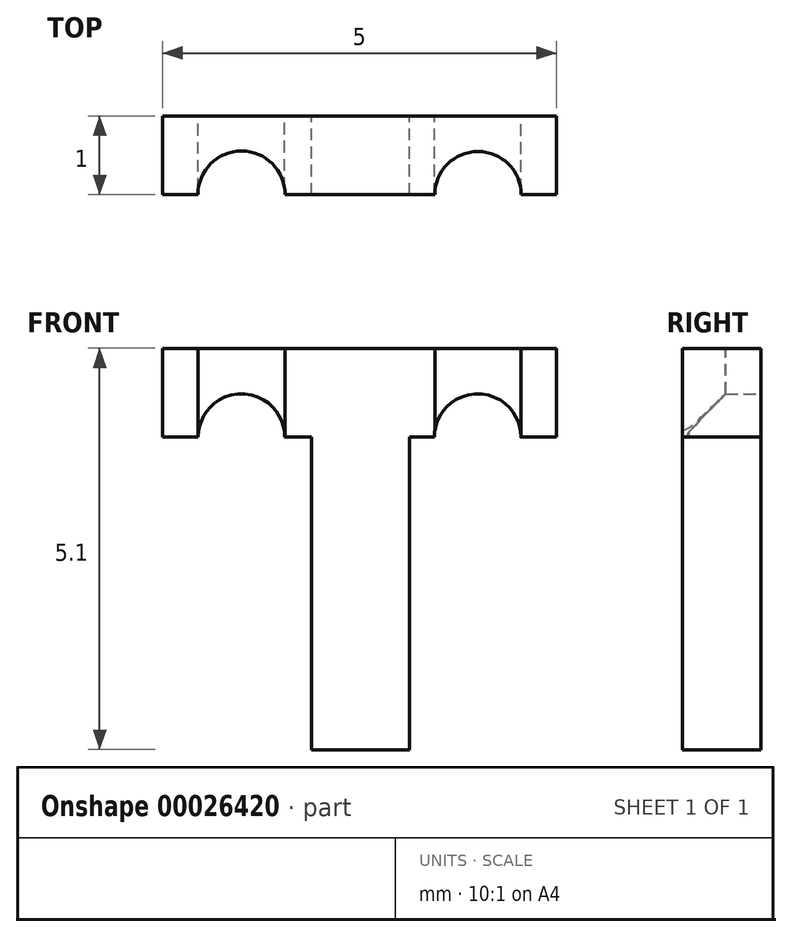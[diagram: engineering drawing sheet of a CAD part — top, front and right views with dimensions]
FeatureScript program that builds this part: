
annotation { "Feature Type Name" : "Feature", "Feature Type Description" : "" }
export const myFeature = defineFeature(function(context is Context, id is Id, definition is map)
    precondition{}
    {
        {
            var Q0;
            Q0=qCreatedBy(makeId("Front.planeOp"),FACE);
            var sketch = newSketch(context, id + "F0", { "sketchPlane" : qUnion([Q0])});
            skArc(sketch, "E0", {"start": v(-0.95, 0) * mm, "mid": v(-1.5, 0.55) * mm, "end": v(-2.05, 0) * mm});
            skArc(sketch, "E1", {"start": v(2.05, 0) * mm, "mid": v(1.5, 0.55) * mm, "end": v(0.95, 0) * mm});
            skLineSegment(sketch, "E2.bottom", {"start": v(-2.5, 0) * mm, "end": v(-2.05, 0) * mm});
            skLineSegment(sketch, "E2.top", {"start": v(-2.5, 1.13) * mm, "end": v(2.5, 1.13) * mm});
            skLineSegment(sketch, "E2.left", {"start": v(-2.5, 0) * mm, "end": v(-2.5, 1.13) * mm});
            skLineSegment(sketch, "E2.right", {"start": v(2.5, 0) * mm, "end": v(2.5, 1.13) * mm});
            skLineSegment(sketch, "E3.top", {"start": v(-0.61, -3.97) * mm, "end": v(0.64, -3.97) * mm});
            skLineSegment(sketch, "E3.left", {"start": v(-0.61, 0) * mm, "end": v(-0.61, -3.97) * mm});
            skLineSegment(sketch, "E3.right", {"start": v(0.64, 0) * mm, "end": v(0.64, -3.97) * mm});
            skLineSegment(sketch, "E4.trimOffspring", {"start": v(0.64, 0) * mm, "end": v(0.95, 0) * mm});
            skLineSegment(sketch, "E5.trimOffspring", {"start": v(2.05, 0) * mm, "end": v(2.5, 0) * mm});
            skLineSegment(sketch, "E6.trimOffspring", {"start": v(-0.95, 0) * mm, "end": v(-0.61, 0) * mm});
            skSolve(sketch);
        }
        {
            var Q0;
            Q0 = qSketchRegion(id + "F0", true);
            extrude(context, id + "F1", {"entities" : qUnion([Q0]), "depth" : 1 * mm});
        }
        {
            var Q0;
            Q0=makeQuery(id+"F1.opExtrude","SWEPT_FACE",FACE,{"disambiguationData":[OSD([sQuery(id+"F0.wireOp",EDGE,"E2.top")])]});
            var sketch = newSketch(context, id + "F2", { "sketchPlane" : qUnion([Q0])});
            skArc(sketch, "E7", {"start": v(-0.95, -1) * mm, "mid": v(-1.5, -0.45) * mm, "end": v(-2.05, -1) * mm});
            skArc(sketch, "E8", {"start": v(2.05, -1) * mm, "mid": v(1.5, -0.45) * mm, "end": v(0.96, -1) * mm});
            skLineSegment(sketch, "E9", {"start": v(-2.05, -1) * mm, "end": v(-0.95, -1) * mm});
            skLineSegment(sketch, "E10", {"start": v(0.96, -1) * mm, "end": v(2.05, -1) * mm});
            skSolve(sketch);
        }
        {
            var Q0;
            Q0 = qSketchRegion(id + "F2", true);
            extrude(context, id + "F3", {"entities" : qUnion([Q0]), "operationType" : NewBodyOperationType.REMOVE, "oppositeDirection" : true, "depth" : 25 * mm});
        }
    });
